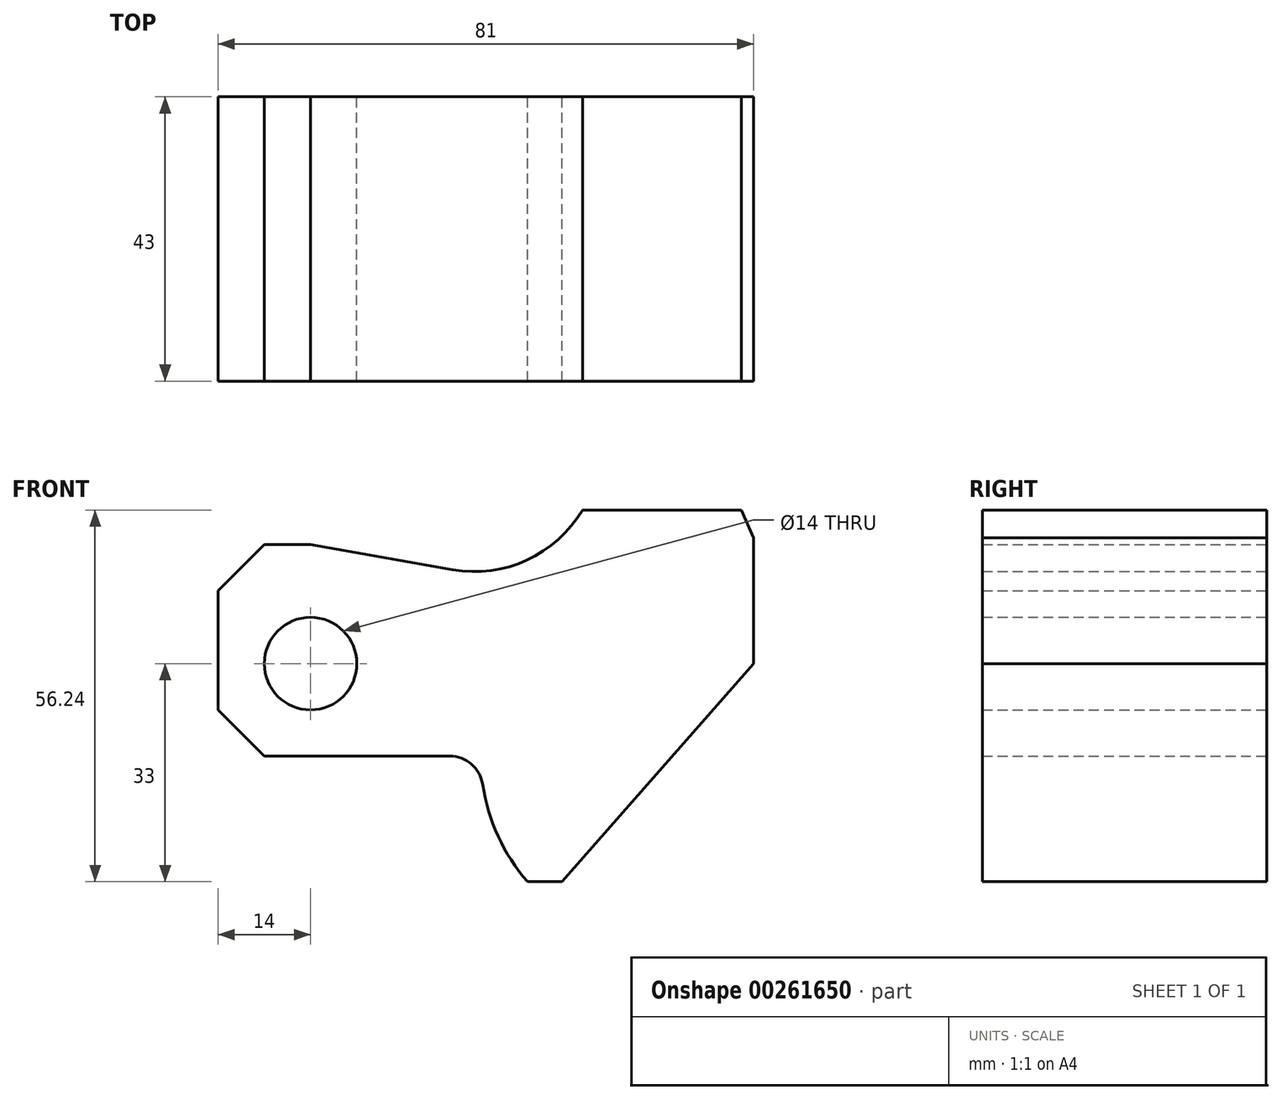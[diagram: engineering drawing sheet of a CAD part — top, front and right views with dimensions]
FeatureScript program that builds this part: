
annotation { "Feature Type Name" : "Feature", "Feature Type Description" : "" }
export const myFeature = defineFeature(function(context is Context, id is Id, definition is map)
    precondition{}
    {
        {
            var Q0;
            Q0=qCreatedBy(makeId("Front.planeOp"),FACE);
            var sketch = newSketch(context, id + "F0", { "sketchPlane" : qUnion([Q0])});
            skCircle(sketch, "E0", {"center": v(0, 0) * mm, "radius": 7 * mm});
            skLineSegment(sketch, "E1", {"start": v(-14, 11) * mm, "end": v(-14, -7) * mm});
            skLineSegment(sketch, "E2", {"start": v(0, 0) * mm, "end": v(-29.59, 0) * mm});
            skLineSegment(sketch, "E3", {"start": v(-7, 18) * mm, "end": v(0, 18) * mm});
            skLineSegment(sketch, "E4", {"start": v(-14, 11) * mm, "end": v(-7, 18) * mm});
            skLineSegment(sketch, "E5", {"start": v(-7, -14) * mm, "end": v(0, -14) * mm});
            skLineSegment(sketch, "E6", {"start": v(-7, -14) * mm, "end": v(-14, -7) * mm});
            skLineSegment(sketch, "E7", {"start": v(67, 19) * mm, "end": v(67, 0) * mm});
            skLineSegment(sketch, "E8", {"start": v(65.13, 23.24) * mm, "end": v(41.13, 23.24) * mm});
            skLineSegment(sketch, "E9", {"start": v(65.13, 23.24) * mm, "end": v(67, 19) * mm});
            skLineSegment(sketch, "E10", {"start": v(67, 0) * mm, "end": v(38, -33) * mm});
            skPoint(sketch, "E11", {"position": v(54.7, -14) * mm});
            skLineSegment(sketch, "E12", {"start": v(38, -33) * mm, "end": v(32.79, -33) * mm});
            skLineSegment(sketch, "E13", {"start": v(0, -14) * mm, "end": v(21.07, -14) * mm});
            skArc(sketch, "E14", {"start": v(32.79, -33) * mm, "mid": v(28.35, -26.12) * mm, "end": v(26.01, -18.26) * mm});
            skArc(sketch, "E15", {"start": v(21.48, 14.21) * mm, "mid": v(32.71, 15.66) * mm, "end": v(41.13, 23.24) * mm});
            skLineSegment(sketch, "E16", {"start": v(0, 18) * mm, "end": v(21.48, 14.21) * mm});
            skPoint(sketch, "E17.orphan", {"position": v(8.43, 23.24) * mm});
            skPoint(sketch, "E18.visualSharp", {"position": v(25.7, -14) * mm});
            skArc(sketch, "E18.filletArc", {"start": v(26.01, -18.26) * mm, "mid": v(24.33, -15.21) * mm, "end": v(21.07, -14) * mm});
            skSolve(sketch);
        }
        {
            var Q0;
            Q0 = qSketchRegion(id + "F0", true);
            extrude(context, id + "F1", {"entities" : qUnion([Q0]), "depth" : 43 * mm});
        }
    });
